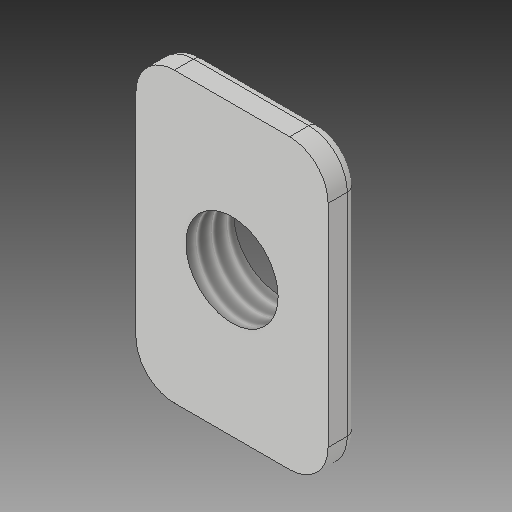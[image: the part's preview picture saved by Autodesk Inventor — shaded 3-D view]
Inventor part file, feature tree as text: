
AUTODESK INVENTOR PART (.ipt)
format: ipt  version: 2018 (Build 220112000, 112)  size: 159,232 bytes
history: native  units: mm
features: other x3, sketch x2
ambient origin geometry x8: Origin, YZ Plane, XZ Plane, XY Plane, X Axis, Y Axis, Z Axis, Center Point
bodies: Solid1 (feature_tree)
feature tree (5):
  other  "M5 Tee Nut-Generic.ipt"
  other  "Solid1::M5 Tee Nut-Generic.ipt"
  other  "TaggingFeature1"
  sketch  "Sketch1"  dims[d0=10.0mm]
  sketch  "Sketch2"
